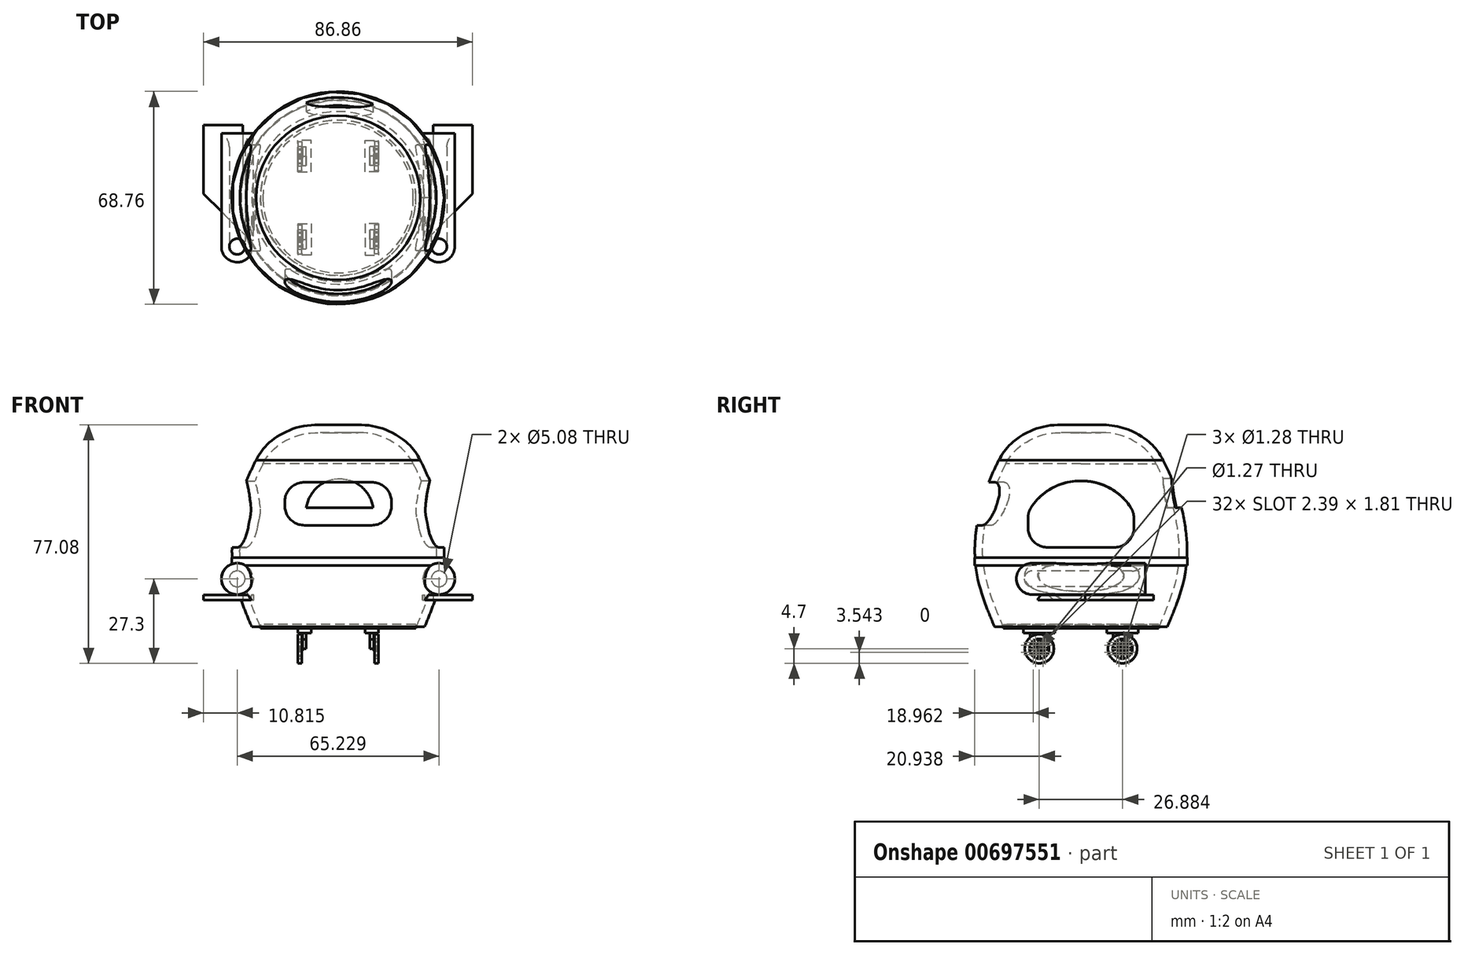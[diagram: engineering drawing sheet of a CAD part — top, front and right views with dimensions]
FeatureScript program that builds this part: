
annotation { "Feature Type Name" : "Feature", "Feature Type Description" : "" }
export const myFeature = defineFeature(function(context is Context, id is Id, definition is map)
    precondition{}
    {
        {
            var Q0;
            Q0=qCreatedBy(makeId("Front.planeOp"),FACE);
            var sketch = newSketch(context, id + "F0", { "sketchPlane" : qUnion([Q0])});
            skFitSpline(sketch, "E0", {"points": [v(-26.52, 28.24) * mm, v(-31.57, 16.07) * mm, v(-34.1, -5.28) * mm, v(-27.9, -25.71) * mm], "startDerivative": vector(-19.07, -39.25) * mm, "endDerivative": vector(23, -55.14) * mm});
            skLineSegment(sketch, "E1", {"start": v(0, 51.66) * mm, "end": v(0, -63.37) * mm, "construction": true});
            skLineSegment(sketch, "E2", {"start": v(0, 43.62) * mm, "end": v(0, -25.71) * mm});
            skFitSpline(sketch, "E3", {"points": [v(-26.52, 28.24) * mm, v(-24.68, 31.2) * mm, v(-21.66, 34.36) * mm, v(-16.76, 37.41) * mm, v(-10.13, 39.4) * mm, v(-3.92, 39.57) * mm, v(0, 39.62) * mm], "startDerivative": vector(11.97, 21.05) * mm, "endDerivative": vector(33.65, 0.28) * mm});
            skLineSegment(sketch, "E4", {"start": v(-27.9, -25.71) * mm, "end": v(0, -25.71) * mm});
            skSolve(sketch);
        }
        {
            var Q0;
            Q0=makeQuery(id+"F0.imprint","IMPRINT",FACE,{"disambiguationData":[TD([[makeQuery(id+"F0.imprint","IMPRINT",EDGE,{"derivedFrom":sQuery(id+"F0.wireOp",EDGE,"E0")}),1.0]])]});
            var Q1;
            Q1=sQuery(id+"F0.wireOp",EDGE,"E2");
            revolve(context, id + "F1", {"entities" : qUnion([Q0]), "axis" : qUnion([Q1]), "revolveType" : RevolveType.FULL});
        }
        {
            var Q0;
            Q0=makeQuery(id+"F1.opRevolve","SWEPT_FACE",FACE,{"disambiguationData":[OSD([sQuery(id+"F0.wireOp",EDGE,"E4")])]});
            shell(context, id + "F2", {"entities" : qUnion([Q0]), "thickness" : 2.54 * mm});
        }
        {
            var Q0;
            Q0=qCreatedBy(makeId("Top.planeOp"),FACE);
            cPlane(context, id + "F3", {"entities" : qUnion([Q0]), "cplaneType" : CPlaneType.OFFSET, "offset" : 26.16 * mm, "oppositeDirection" : true, "width" : 152.4 * mm, "height" : 152.4 * mm});
        }
        {
            var Q0;
            Q0=qCreatedBy(id+"F3.planeOp",FACE);
            var sketch = newSketch(context, id + "F4", { "sketchPlane" : qUnion([Q0])});
            skPoint(sketch, "E5.middle", {"position": v(0, 0) * mm});
            skCircle(sketch, "E6", {"center": v(0, 0) * mm, "radius": 25.04 * mm});
            skSolve(sketch);
        }
        {
            var Q0;
            Q0=qCreatedBy(makeId("Front.planeOp"),FACE);
            cPlane(context, id + "F5", {"entities" : qUnion([Q0]), "cplaneType" : CPlaneType.OFFSET, "offset" : 28.45 * mm, "width" : 152.4 * mm, "height" : 152.4 * mm});
        }
        {
            var Q0;
            Q0=qCreatedBy(id+"F5.planeOp",FACE);
            var sketch = newSketch(context, id + "F6", { "sketchPlane" : qUnion([Q0])});
            skLineSegment(sketch, "E7.bottom", {"start": v(-10.9, 21.05) * mm, "end": v(10.9, 21.05) * mm});
            skLineSegment(sketch, "E7.top", {"start": v(-10.9, 7.16) * mm, "end": v(10.9, 7.16) * mm});
            skLineSegment(sketch, "E7.left", {"start": v(-17.26, 14.7) * mm, "end": v(-17.26, 13.51) * mm});
            skLineSegment(sketch, "E7.right", {"start": v(17.26, 14.7) * mm, "end": v(17.26, 13.51) * mm});
            skPoint(sketch, "E7.middle", {"position": v(0, 14.1) * mm});
            skPoint(sketch, "E8.visualSharp", {"position": v(-17.26, 21.05) * mm});
            skArc(sketch, "E8.filletArc", {"start": v(-10.9, 21.05) * mm, "mid": v(-15.4, 19.19) * mm, "end": v(-17.26, 14.7) * mm});
            skPoint(sketch, "E9.visualSharp", {"position": v(17.26, 21.05) * mm});
            skArc(sketch, "E9.filletArc", {"start": v(17.26, 14.7) * mm, "mid": v(15.4, 19.19) * mm, "end": v(10.9, 21.05) * mm});
            skPoint(sketch, "E10.visualSharp", {"position": v(17.26, 7.16) * mm});
            skArc(sketch, "E10.filletArc", {"start": v(10.9, 7.16) * mm, "mid": v(15.4, 9.02) * mm, "end": v(17.26, 13.51) * mm});
            skPoint(sketch, "E11.visualSharp", {"position": v(-17.26, 7.16) * mm});
            skArc(sketch, "E11.filletArc", {"start": v(-17.26, 13.51) * mm, "mid": v(-15.4, 9.02) * mm, "end": v(-10.9, 7.16) * mm});
            skSolve(sketch);
        }
        {
            var Q0;
            Q0 = qSketchRegion(id + "F6", true);
            extrude(context, id + "F7", {"entities" : qUnion([Q0]), "operationType" : NewBodyOperationType.REMOVE, "endBound" : BoundingType.SYMMETRIC, "oppositeDirection" : true, "depth" : 12.7 * mm, "offsetDistance" : 25.4 * mm});
        }
        {
            var Q0;
            Q0=qCreatedBy(makeId("Right.planeOp"),FACE);
            cPlane(context, id + "F8", {"entities" : qUnion([Q0]), "cplaneType" : CPlaneType.OFFSET, "offset" : 30.48 * mm, "width" : 152.4 * mm, "height" : 152.4 * mm});
        }
        {
            var Q0;
            Q0=qCreatedBy(id+"F8.planeOp",FACE);
            var sketch = newSketch(context, id + "F9", { "sketchPlane" : qUnion([Q0])});
            skArc(sketch, "E12", {"start": v(0, 21.5) * mm, "mid": v(-9.18, 19.27) * mm, "end": v(-16.1, 12.86) * mm});
            skArc(sketch, "E13.MirrorCS", {"start": v(0, 21.5) * mm, "mid": v(9.18, 19.27) * mm, "end": v(16.1, 12.86) * mm});
            skLineSegment(sketch, "E14", {"start": v(-17.11, 9.43) * mm, "end": v(-17.11, 6.35) * mm});
            skLineSegment(sketch, "E15", {"start": v(-10.76, 0) * mm, "end": v(10.76, 0) * mm});
            skLineSegment(sketch, "E16", {"start": v(17.11, 6.35) * mm, "end": v(17.11, 9.43) * mm});
            skLineSegment(sketch, "E17.bottom", {"start": v(0.3, 21.5) * mm, "end": v(-0.3, 21.5) * mm});
            skLineSegment(sketch, "E17.top", {"start": v(0.3, 0) * mm, "end": v(-0.3, 0) * mm});
            skPoint(sketch, "E17.middle", {"position": v(0, 10.75) * mm});
            skPoint(sketch, "E18.visualSharp", {"position": v(-17.11, 11.09) * mm});
            skArc(sketch, "E18.filletArc", {"start": v(-16.1, 12.86) * mm, "mid": v(-16.86, 11.22) * mm, "end": v(-17.11, 9.43) * mm});
            skPoint(sketch, "E19.visualSharp", {"position": v(17.11, 11.09) * mm});
            skArc(sketch, "E19.filletArc", {"start": v(17.11, 9.43) * mm, "mid": v(16.86, 11.22) * mm, "end": v(16.1, 12.86) * mm});
            skPoint(sketch, "E20.visualSharp", {"position": v(-17.11, 0) * mm});
            skArc(sketch, "E20.filletArc", {"start": v(-17.11, 6.35) * mm, "mid": v(-15.25, 1.86) * mm, "end": v(-10.76, 0) * mm});
            skPoint(sketch, "E21.visualSharp", {"position": v(17.11, 0) * mm});
            skArc(sketch, "E21.filletArc", {"start": v(10.76, 0) * mm, "mid": v(15.25, 1.86) * mm, "end": v(17.11, 6.35) * mm});
            skSolve(sketch);
        }
        {
            var Q0;
            Q0=makeQuery(id+"F9.imprint","IMPRINT",FACE,{"disambiguationData":[TD([[makeQuery(id+"F9.imprint","IMPRINT",EDGE,{"derivedFrom":sQuery(id+"F9.wireOp",EDGE,"E14")}),1.0]])]});
            extrude(context, id + "F10", {"entities" : qUnion([Q0]), "operationType" : NewBodyOperationType.REMOVE, "endBound" : BoundingType.SYMMETRIC, "depth" : 10.87 * mm, "offsetDistance" : 25.4 * mm});
        }
        {
            var Q0;
            Q0=qCreatedBy(makeId("Right.planeOp"),FACE);
            cPlane(context, id + "F11", {"entities" : qUnion([Q0]), "cplaneType" : CPlaneType.OFFSET, "offset" : 30.48 * mm, "oppositeDirection" : true, "width" : 152.4 * mm, "height" : 152.4 * mm});
        }
        {
            var Q0;
            Q0=qCreatedBy(id+"F11.planeOp",FACE);
            var sketch = newSketch(context, id + "F12", { "sketchPlane" : qUnion([Q0])});
            skArc(sketch, "E22", {"start": v(0.24, 21.49) * mm, "mid": v(-9.07, 19.32) * mm, "end": v(-16.1, 12.85) * mm});
            skArc(sketch, "E23.MirrorCS", {"start": v(-0.24, 21.49) * mm, "mid": v(9.07, 19.32) * mm, "end": v(16.1, 12.85) * mm});
            skLineSegment(sketch, "E24", {"start": v(-17.11, 9.42) * mm, "end": v(-17.11, 6.34) * mm});
            skLineSegment(sketch, "E25", {"start": v(-10.76, -0.01) * mm, "end": v(10.76, -0.01) * mm});
            skLineSegment(sketch, "E26", {"start": v(17.11, 6.34) * mm, "end": v(17.11, 9.42) * mm});
            skLineSegment(sketch, "E27.bottom", {"start": v(0.3, 21.5) * mm, "end": v(-0.3, 21.5) * mm});
            skLineSegment(sketch, "E27.top", {"start": v(0.3, -0.01) * mm, "end": v(-0.3, -0.01) * mm});
            skPoint(sketch, "E27.middle", {"position": v(0, 10.74) * mm});
            skPoint(sketch, "E28.visualSharp", {"position": v(-17.11, 11.08) * mm});
            skArc(sketch, "E28.filletArc", {"start": v(-16.1, 12.85) * mm, "mid": v(-16.86, 11.2) * mm, "end": v(-17.11, 9.42) * mm});
            skPoint(sketch, "E29.visualSharp", {"position": v(17.11, 11.08) * mm});
            skArc(sketch, "E29.filletArc", {"start": v(17.11, 9.42) * mm, "mid": v(16.86, 11.2) * mm, "end": v(16.1, 12.85) * mm});
            skPoint(sketch, "E30.visualSharp", {"position": v(-17.11, -0.01) * mm});
            skArc(sketch, "E30.filletArc", {"start": v(-17.11, 6.34) * mm, "mid": v(-15.25, 1.85) * mm, "end": v(-10.76, -0.01) * mm});
            skPoint(sketch, "E31.visualSharp", {"position": v(17.11, -0.01) * mm});
            skArc(sketch, "E31.filletArc", {"start": v(10.76, -0.01) * mm, "mid": v(15.25, 1.85) * mm, "end": v(17.11, 6.34) * mm});
            skSolve(sketch);
        }
        {
            var Q0;
            Q0 = qSketchRegion(id + "F12", true);
            extrude(context, id + "F13", {"entities" : qUnion([Q0]), "operationType" : NewBodyOperationType.REMOVE, "endBound" : BoundingType.SYMMETRIC, "oppositeDirection" : true, "depth" : 10.87 * mm, "offsetDistance" : 25.4 * mm});
        }
        {
            var Q0;
            Q0=qCreatedBy(makeId("Front.planeOp"),FACE);
            var sketch = newSketch(context, id + "F14", { "sketchPlane" : qUnion([Q0])});
            skLineSegment(sketch, "E32", {"start": v(0, 0) * mm, "end": v(0, -10.16) * mm, "construction": true});
            skCircle(sketch, "E33", {"center": v(-32.61, -10.16) * mm, "radius": 5.08 * mm});
            skCircle(sketch, "E34.MirrorC", {"center": v(32.61, -10.16) * mm, "radius": 5.08 * mm});
            skSolve(sketch);
        }
        {
            var Q0;
            Q0 = qSketchRegion(id + "F14", true);
            extrude(context, id + "F15", {"entities" : qUnion([Q0]), "operationType" : NewBodyOperationType.ADD, "endBound" : BoundingType.SYMMETRIC, "oppositeDirection" : true, "depth" : 41.66 * mm, "offsetDistance" : 25.4 * mm});
        }
        {
            var Q0;
            Q0=makeQuery(id+"F15.opExtrude","CAP_EDGE",EDGE,{"disambiguationData":[OSD([sQuery(id+"F14.wireOp",EDGE,"E33")])],"isStart":true});
            fillet(context, id + "F16", {"entities" : qUnion([Q0]), "radius" : 5.08 * mm, "tangentPropagation" : true, "allowEdgeOverflow" : false});
        }
        {
            var Q0;
            Q0=makeQuery(id+"F15.opExtrude","CAP_EDGE",EDGE,{"disambiguationData":[OSD([sQuery(id+"F14.wireOp",EDGE,"E34.MirrorC")])],"isStart":true});
            fillet(context, id + "F17", {"entities" : qUnion([Q0]), "radius" : 5.08 * mm, "tangentPropagation" : true, "allowEdgeOverflow" : false});
        }
        {
            var Q0;
            Q0=makeQuery(id+"F15.opExtrude","CAP_FACE",FACE,{"disambiguationData":[OSD([sQuery(id+"F14.wireOp",EDGE,"E34.MirrorC")])],"isStart":false});
            var Q1;
            Q1=makeQuery(id+"F15.opExtrude","CAP_FACE",FACE,{"disambiguationData":[OSD([sQuery(id+"F14.wireOp",EDGE,"E33")])],"isStart":false});
            shell(context, id + "F18", {"entities" : qUnion([Q0, Q1]), "thickness" : 2.54 * mm});
        }
        {
            var Q0;
            {var subQ0=sQuery(id+"F14.wireOp",EDGE,"E34.MirrorC");Q0=makeQuery(id+"F18.opShell","OFFSET_EDGE",EDGE,{"disambiguationData":[OSD([subQ0]),TDD([makeQuery(id+"F15.opExtrude","CAP_EDGE",EDGE,{"disambiguationData":[OSD([subQ0])],"isStart":false})])]});}
            var Q1;
            {var subQ0=sQuery(id+"F14.wireOp",EDGE,"E33");Q1=makeQuery(id+"F18.opShell","OFFSET_EDGE",EDGE,{"disambiguationData":[OSD([subQ0]),TDD([makeQuery(id+"F15.opExtrude","CAP_EDGE",EDGE,{"disambiguationData":[OSD([subQ0])],"isStart":false})])]});}
            fillet(context, id + "F19", {"entities" : qUnion([Q0, Q1]), "radius" : 5.08 * mm, "tangentPropagation" : true, "allowEdgeOverflow" : false});
        }
        {
            var Q0;
            Q0=qCreatedBy(makeId("Top.planeOp"),FACE);
            cPlane(context, id + "F20", {"entities" : qUnion([Q0]), "cplaneType" : CPlaneType.OFFSET, "offset" : 15 * mm, "oppositeDirection" : true, "width" : 152.4 * mm, "height" : 152.4 * mm});
        }
        {
            var Q0;
            Q0 = qSketchRegion(id + "F4", true);
            extrude(context, id + "F21", {"entities" : qUnion([Q0]), "depth" : 1.27 * mm, "offsetDistance" : 25.4 * mm});
        }
        {
            var Q0;
            Q0=qCreatedBy(id+"F3.planeOp",FACE);
            var sketch = newSketch(context, id + "F22", { "sketchPlane" : qUnion([Q0])});
            skLineSegment(sketch, "E35.MirrorCS", {"start": v(-8.75, -18.52) * mm, "end": v(-13, -18.52) * mm});
            skLineSegment(sketch, "E36", {"start": v(-13, -8.36) * mm, "end": v(-8.75, -8.36) * mm});
            skLineSegment(sketch, "E37.trimOffspring", {"start": v(-8.75, -8.36) * mm, "end": v(-8.75, -18.52) * mm});
            skLineSegment(sketch, "E38.trimOffspring", {"start": v(-13, -8.36) * mm, "end": v(-13, -18.52) * mm});
            skLineSegment(sketch, "E39.MirrorCS", {"start": v(8.75, -8.36) * mm, "end": v(8.75, -18.52) * mm});
            skLineSegment(sketch, "E40.MirrorCS", {"start": v(13, -8.36) * mm, "end": v(13, -18.52) * mm});
            skLineSegment(sketch, "E41.MirrorCS", {"start": v(8.75, -18.52) * mm, "end": v(13, -18.52) * mm});
            skLineSegment(sketch, "E42.MirrorCS", {"start": v(13, -8.36) * mm, "end": v(8.75, -8.36) * mm});
            skLineSegment(sketch, "E43.MirrorCS", {"start": v(-13, 8.36) * mm, "end": v(-8.75, 8.36) * mm});
            skLineSegment(sketch, "E44.MirrorCS", {"start": v(-8.75, 18.52) * mm, "end": v(-13, 18.52) * mm});
            skLineSegment(sketch, "E45.MirrorCS", {"start": v(-13, 8.36) * mm, "end": v(-13, 18.52) * mm});
            skLineSegment(sketch, "E46.MirrorCS", {"start": v(-8.75, 8.36) * mm, "end": v(-8.75, 18.52) * mm});
            skLineSegment(sketch, "E47.MirrorCS", {"start": v(8.75, 8.36) * mm, "end": v(8.75, 18.52) * mm});
            skLineSegment(sketch, "E48.MirrorCS", {"start": v(8.75, 18.52) * mm, "end": v(13, 18.52) * mm});
            skLineSegment(sketch, "E49.MirrorCS", {"start": v(13, 8.36) * mm, "end": v(13, 18.52) * mm});
            skLineSegment(sketch, "E50.MirrorCS", {"start": v(13, 8.36) * mm, "end": v(8.75, 8.36) * mm});
            skSolve(sketch);
        }
        {
            var Q0;
            Q0 = qSketchRegion(id + "F22", true);
            extrude(context, id + "F23", {"entities" : qUnion([Q0]), "operationType" : NewBodyOperationType.ADD, "oppositeDirection" : true, "depth" : 1.52 * mm, "offsetDistance" : 25.4 * mm});
        }
        {
            var Q0;
            Q0=makeQuery(id+"F23.opExtrude","CAP_FACE",FACE,{"disambiguationData":[OSD([sQuery(id+"F22.wireOp",EDGE,"E35.MirrorCS"),sQuery(id+"F22.wireOp",EDGE,"E36"),sQuery(id+"F22.wireOp",EDGE,"E37.trimOffspring"),sQuery(id+"F22.wireOp",EDGE,"E38.trimOffspring")])],"isStart":false});
            var sketch = newSketch(context, id + "F24", { "sketchPlane" : qUnion([Q0])});
            skLineSegment(sketch, "E51.bottom", {"start": v(-11.45, 10.4) * mm, "end": v(-10.3, 10.4) * mm});
            skLineSegment(sketch, "E51.top", {"start": v(-11.45, 16.48) * mm, "end": v(-10.3, 16.48) * mm});
            skLineSegment(sketch, "E51.left", {"start": v(-11.45, 10.4) * mm, "end": v(-11.45, 16.48) * mm});
            skLineSegment(sketch, "E51.right", {"start": v(-10.3, 10.4) * mm, "end": v(-10.3, 16.48) * mm});
            skPoint(sketch, "E51.middle", {"position": v(-10.87, 13.44) * mm});
            skPoint(sketch, "E51.middle.positionSnap0", {"position": v(-10.87, 18.52) * mm});
            skPoint(sketch, "E51.middle.positionSnap1", {"position": v(-13, 13.44) * mm});
            skPoint(sketch, "E51.centerSnap0", {"position": v(-10.87, 18.52) * mm});
            skPoint(sketch, "E52.MirrorP", {"position": v(-10.87, -13.44) * mm});
            skLineSegment(sketch, "E53.MirrorCS", {"start": v(-11.45, -10.4) * mm, "end": v(-11.45, -16.48) * mm});
            skLineSegment(sketch, "E54.MirrorCS", {"start": v(-11.45, -10.4) * mm, "end": v(-10.3, -10.4) * mm});
            skLineSegment(sketch, "E55.MirrorCS", {"start": v(-10.3, -10.4) * mm, "end": v(-10.3, -16.48) * mm});
            skLineSegment(sketch, "E56.MirrorCS", {"start": v(-11.45, -16.48) * mm, "end": v(-10.3, -16.48) * mm});
            skLineSegment(sketch, "E57.MirrorCS", {"start": v(10.3, 10.4) * mm, "end": v(10.3, 16.48) * mm});
            skLineSegment(sketch, "E58.MirrorCS", {"start": v(11.45, 10.4) * mm, "end": v(11.45, 16.48) * mm});
            skLineSegment(sketch, "E59.MirrorCS", {"start": v(11.45, 10.4) * mm, "end": v(10.3, 10.4) * mm});
            skLineSegment(sketch, "E60.MirrorCS", {"start": v(11.45, 16.48) * mm, "end": v(10.3, 16.48) * mm});
            skLineSegment(sketch, "E61.MirrorCS", {"start": v(11.45, -10.4) * mm, "end": v(10.3, -10.4) * mm});
            skLineSegment(sketch, "E62.MirrorCS", {"start": v(11.45, -16.48) * mm, "end": v(10.3, -16.48) * mm});
            skLineSegment(sketch, "E63.MirrorCS", {"start": v(11.45, -10.4) * mm, "end": v(11.45, -16.48) * mm});
            skLineSegment(sketch, "E64.MirrorCS", {"start": v(10.3, -10.4) * mm, "end": v(10.3, -16.48) * mm});
            skSolve(sketch);
        }
        {
            var Q0;
            Q0 = qSketchRegion(id + "F24", true);
            extrude(context, id + "F25", {"entities" : qUnion([Q0]), "operationType" : NewBodyOperationType.ADD, "depth" : 5.08 * mm, "offsetDistance" : 25.4 * mm});
        }
        {
            var Q0;
            Q0=makeQuery(id+"F25.opExtrude","CAP_EDGE",EDGE,{"disambiguationData":[OSD([sQuery(id+"F24.wireOp",EDGE,"E54.MirrorCS")])],"isStart":false});
            var Q1;
            Q1=makeQuery(id+"F25.opExtrude","CAP_EDGE",EDGE,{"disambiguationData":[OSD([sQuery(id+"F24.wireOp",EDGE,"E56.MirrorCS")])],"isStart":false});
            var Q2;
            Q2=makeQuery(id+"F25.opExtrude","CAP_EDGE",EDGE,{"disambiguationData":[OSD([sQuery(id+"F24.wireOp",EDGE,"E51.top")])],"isStart":false});
            var Q3;
            Q3=makeQuery(id+"F25.opExtrude","CAP_EDGE",EDGE,{"disambiguationData":[OSD([sQuery(id+"F24.wireOp",EDGE,"E51.bottom")])],"isStart":false});
            var Q4;
            Q4=makeQuery(id+"F25.opExtrude","CAP_EDGE",EDGE,{"disambiguationData":[OSD([sQuery(id+"F24.wireOp",EDGE,"E62.MirrorCS")])],"isStart":false});
            var Q5;
            Q5=makeQuery(id+"F25.opExtrude","CAP_EDGE",EDGE,{"disambiguationData":[OSD([sQuery(id+"F24.wireOp",EDGE,"E61.MirrorCS")])],"isStart":false});
            var Q6;
            Q6=makeQuery(id+"F25.opExtrude","CAP_EDGE",EDGE,{"disambiguationData":[OSD([sQuery(id+"F24.wireOp",EDGE,"E59.MirrorCS")])],"isStart":false});
            var Q7;
            Q7=makeQuery(id+"F25.opExtrude","CAP_EDGE",EDGE,{"disambiguationData":[OSD([sQuery(id+"F24.wireOp",EDGE,"E60.MirrorCS")])],"isStart":false});
            chamfer(context, id + "F26", {"entities" : qUnion([Q0, Q1, Q2, Q3, Q4, Q5, Q6, Q7]), "width" : 3.05 * mm, "tangentPropagation" : true});
        }
        {
            var Q0;
            Q0=makeQuery(id+"F25.opExtrude","SWEPT_FACE",FACE,{"disambiguationData":[OSD([sQuery(id+"F24.wireOp",EDGE,"E51.left")])]});
            var sketch = newSketch(context, id + "F27", { "sketchPlane" : qUnion([Q0])});
            skCircle(sketch, "E65", {"center": v(13.44, -32.76) * mm, "radius": 0.64 * mm});
            skSolve(sketch);
        }
        {
            var Q0;
            Q0 = qSketchRegion(id + "F27", true);
            extrude(context, id + "F28", {"entities" : qUnion([Q0]), "operationType" : NewBodyOperationType.ADD, "depth" : 0.25 * mm, "offsetDistance" : 25.4 * mm});
        }
        {
            var Q0;
            Q0=makeQuery(id+"F28.opExtrude","CAP_FACE",FACE,{"disambiguationData":[OSD([sQuery(id+"F27.wireOp",EDGE,"E65")])],"isStart":false});
            var sketch = newSketch(context, id + "F29", { "sketchPlane" : qUnion([Q0])});
            skCircle(sketch, "E66", {"center": v(13.44, -32.76) * mm, "radius": 4.7 * mm});
            skArc(sketch, "E67.0", {"start": v(13.19, -29.6) * mm, "mid": v(12.23, -29.82) * mm, "end": v(11.38, -30.34) * mm});
            skArc(sketch, "E68", {"start": v(13.19, -31.9) * mm, "mid": v(13.1, -31.94) * mm, "end": v(13.02, -31.98) * mm});
            skLineSegment(sketch, "E69.0", {"start": v(13.7, -31.9) * mm, "end": v(13.7, -29.6) * mm});
            skLineSegment(sketch, "E70.0", {"start": v(13.19, -31.9) * mm, "end": v(13.19, -29.6) * mm});
            skLineSegment(sketch, "E71", {"start": v(13.7, -33.61) * mm, "end": v(13.7, -35.93) * mm});
            skLineSegment(sketch, "E72", {"start": v(13.19, -33.61) * mm, "end": v(13.19, -35.93) * mm});
            skArc(sketch, "E73.trimOffspring", {"start": v(13.7, -33.61) * mm, "mid": v(13.78, -33.58) * mm, "end": v(13.87, -33.54) * mm});
            skArc(sketch, "E74.trimOffspring", {"start": v(13.7, -35.93) * mm, "mid": v(14.66, -35.7) * mm, "end": v(15.5, -35.18) * mm});
            skLineSegment(sketch, "E75.0", {"start": v(8.74, -33.01) * mm, "end": v(8.75, -33.01) * mm});
            skLineSegment(sketch, "E76.0", {"start": v(8.74, -32.5) * mm, "end": v(8.75, -32.5) * mm});
            skLineSegment(sketch, "E77.trimOffspring", {"start": v(10.27, -32.5) * mm, "end": v(12.59, -32.5) * mm});
            skLineSegment(sketch, "E78.trimOffspring", {"start": v(10.27, -33.01) * mm, "end": v(12.59, -33.01) * mm});
            skLineSegment(sketch, "E79.trimOffspring", {"start": v(18.14, -32.5) * mm, "end": v(18.14, -32.5) * mm});
            skLineSegment(sketch, "E80.trimOffspring", {"start": v(18.14, -33.01) * mm, "end": v(18.14, -33.01) * mm});
            skLineSegment(sketch, "E81.trimOffspring", {"start": v(14.3, -32.5) * mm, "end": v(16.61, -32.5) * mm});
            skLineSegment(sketch, "E82.trimOffspring", {"start": v(14.3, -33.01) * mm, "end": v(16.61, -33.01) * mm});
            skArc(sketch, "E83.trimOffspring", {"start": v(10.27, -33.01) * mm, "mid": v(10.5, -33.98) * mm, "end": v(11.02, -34.82) * mm});
            skArc(sketch, "E84.trimOffspring", {"start": v(16.61, -32.5) * mm, "mid": v(16.38, -31.54) * mm, "end": v(15.86, -30.7) * mm});
            skArc(sketch, "E85.trimOffspring", {"start": v(12.59, -33.01) * mm, "mid": v(12.62, -33.1) * mm, "end": v(12.66, -33.18) * mm});
            skLineSegment(sketch, "E86.0", {"start": v(15.51, -30.33) * mm, "end": v(13.87, -31.98) * mm});
            skLineSegment(sketch, "E87.0", {"start": v(15.87, -30.7) * mm, "end": v(14.22, -32.34) * mm});
            skLineSegment(sketch, "E88.trimOffspring", {"start": v(12.66, -33.18) * mm, "end": v(11.01, -34.83) * mm});
            skLineSegment(sketch, "E89.trimOffspring", {"start": v(13.02, -33.54) * mm, "end": v(11.37, -35.19) * mm});
            skArc(sketch, "E90.trimOffspring", {"start": v(13.02, -33.54) * mm, "mid": v(13.1, -33.58) * mm, "end": v(13.19, -33.61) * mm});
            skArc(sketch, "E91.trimOffspring", {"start": v(13.87, -31.98) * mm, "mid": v(13.78, -31.94) * mm, "end": v(13.7, -31.9) * mm});
            skArc(sketch, "E92.trimOffspring", {"start": v(11.38, -35.18) * mm, "mid": v(12.23, -35.7) * mm, "end": v(13.19, -35.93) * mm});
            skArc(sketch, "E93.trimOffspring", {"start": v(15.5, -30.34) * mm, "mid": v(14.66, -29.82) * mm, "end": v(13.7, -29.6) * mm});
            skArc(sketch, "E94.trimOffspring", {"start": v(14.3, -32.5) * mm, "mid": v(14.26, -32.42) * mm, "end": v(14.22, -32.34) * mm});
            skLineSegment(sketch, "E95.0", {"start": v(11.01, -30.7) * mm, "end": v(12.66, -32.34) * mm});
            skLineSegment(sketch, "E96.0", {"start": v(11.37, -30.33) * mm, "end": v(13.02, -31.98) * mm});
            skArc(sketch, "E97.trimOffspring", {"start": v(12.66, -32.34) * mm, "mid": v(12.62, -32.42) * mm, "end": v(12.59, -32.5) * mm});
            skLineSegment(sketch, "E98.trimOffspring", {"start": v(13.87, -33.54) * mm, "end": v(15.51, -35.19) * mm});
            skLineSegment(sketch, "E99.trimOffspring", {"start": v(14.22, -33.18) * mm, "end": v(15.87, -34.83) * mm});
            skArc(sketch, "E100.trimOffspring", {"start": v(14.22, -33.18) * mm, "mid": v(14.26, -33.1) * mm, "end": v(14.3, -33.01) * mm});
            skArc(sketch, "E101.trimOffspring", {"start": v(11.02, -30.7) * mm, "mid": v(10.5, -31.54) * mm, "end": v(10.27, -32.5) * mm});
            skArc(sketch, "E102.trimOffspring", {"start": v(15.86, -34.82) * mm, "mid": v(16.38, -33.98) * mm, "end": v(16.61, -33.01) * mm});
            skSolve(sketch);
        }
        {
            var Q0;
            {var subQ16=sQuery(id+"F29.wireOp",EDGE,"E67.0");Q0=makeQuery(id+"F29.imprint","IMPRINT",FACE,{"disambiguationData":[TD([[makeQuery(id+"F29.imprint","IMPRINT",EDGE,{"derivedFrom":subQ16}),-1.0]])]});}
            extrude(context, id + "F30", {"entities" : qUnion([Q0]), "depth" : 1.27 * mm, "offsetDistance" : 25.4 * mm});
        }
        {
            var Q0;
            Q0=qCreatedBy(makeId("Right.planeOp"),FACE);
            cPlane(context, id + "F31", {"entities" : qUnion([Q0]), "cplaneType" : CPlaneType.OFFSET, "offset" : 30.73 * mm, "oppositeDirection" : true, "width" : 152.4 * mm, "height" : 152.4 * mm});
        }
        {
            var Q0;
            Q0=qCreatedBy(id+"F31.planeOp",FACE);
            var sketch = newSketch(context, id + "F32", { "sketchPlane" : qUnion([Q0])});
            skLineSegment(sketch, "E103.bottom", {"start": v(23.47, -15.31) * mm, "end": v(-13.94, -15.31) * mm});
            skLineSegment(sketch, "E103.top", {"start": v(23.47, -16.99) * mm, "end": v(-13.94, -16.99) * mm});
            skLineSegment(sketch, "E103.left", {"start": v(23.47, -15.31) * mm, "end": v(23.47, -16.99) * mm});
            skPoint(sketch, "E103.middle", {"position": v(0, -16.15) * mm});
            skLineSegment(sketch, "E104", {"start": v(-13.94, -15.31) * mm, "end": v(-13.94, -16.99) * mm});
            skSolve(sketch);
        }
        {
            var Q0;
            Q0 = qSketchRegion(id + "F32", true);
            extrude(context, id + "F33", {"entities" : qUnion([Q0]), "operationType" : NewBodyOperationType.ADD, "oppositeDirection" : true, "depth" : 12.7 * mm, "offsetDistance" : 25.4 * mm});
        }
        {
            var Q0;
            {var subQ0=sQuery(id+"F32.wireOp",EDGE,"E103.bottom");var subQ1=sQuery(id+"F32.wireOp",EDGE,"E104");var subQ2=sQuery(id+"F32.wireOp",EDGE,"E103.top");Q0=makeQuery(id+"F33.boolean.opBoolean","SPLIT",FACE,{"disambiguationData":[TD([makeQuery(id+"F33.opExtrude","SWEPT_FACE",FACE,{"disambiguationData":[OSD([subQ1])]})])],"derivedFrom":makeQuery(id+"F33.opExtrude","CAP_FACE",FACE,{"disambiguationData":[OSD([subQ0,subQ2,sQuery(id+"F32.wireOp",EDGE,"E103.left"),subQ1])],"isStart":true})});}
            var sketch = newSketch(context, id + "F34", { "sketchPlane" : qUnion([Q0])});
            skLineSegment(sketch, "E105", {"start": v(-13.94, -15.31) * mm, "end": v(-13.94, -16.99) * mm});
            skLineSegment(sketch, "E106", {"start": v(-13.94, -16.99) * mm, "end": v(-6.12, -16.99) * mm});
            skLineSegment(sketch, "E107", {"start": v(-6.12, -16.99) * mm, "end": v(-8.56, -15.31) * mm});
            skLineSegment(sketch, "E108", {"start": v(-8.56, -15.31) * mm, "end": v(-13.94, -15.31) * mm});
            skSolve(sketch);
        }
        {
            var Q0;
            Q0 = qSketchRegion(id + "F34", true);
            extrude(context, id + "F35", {"entities" : qUnion([Q0]), "operationType" : NewBodyOperationType.ADD, "depth" : 3.48 * mm, "offsetDistance" : 25.4 * mm});
        }
        {
            var Q0;
            Q0=makeQuery(id+"F25.opExtrude","SWEPT_FACE",FACE,{"disambiguationData":[OSD([sQuery(id+"F24.wireOp",EDGE,"E53.MirrorCS")])]});
            var sketch = newSketch(context, id + "F36", { "sketchPlane" : qUnion([Q0])});
            skCircle(sketch, "E109", {"center": v(-13.44, -32.76) * mm, "radius": 0.64 * mm});
            skSolve(sketch);
        }
        {
            var Q0;
            Q0 = qSketchRegion(id + "F36", true);
            extrude(context, id + "F37", {"entities" : qUnion([Q0]), "operationType" : NewBodyOperationType.ADD, "depth" : 0.25 * mm, "offsetDistance" : 25.4 * mm});
        }
        {
            var Q0;
            Q0=makeQuery(id+"F25.opExtrude","SWEPT_FACE",FACE,{"disambiguationData":[OSD([sQuery(id+"F24.wireOp",EDGE,"E63.MirrorCS")])]});
            var sketch = newSketch(context, id + "F38", { "sketchPlane" : qUnion([Q0])});
            skCircle(sketch, "E110", {"center": v(13.44, -32.76) * mm, "radius": 0.64 * mm});
            skSolve(sketch);
        }
        {
            var Q0;
            Q0 = qSketchRegion(id + "F38", true);
            extrude(context, id + "F39", {"entities" : qUnion([Q0]), "operationType" : NewBodyOperationType.ADD, "depth" : 0.25 * mm, "offsetDistance" : 25.4 * mm});
        }
        {
            var Q0;
            Q0=makeQuery(id+"F25.opExtrude","SWEPT_FACE",FACE,{"disambiguationData":[OSD([sQuery(id+"F24.wireOp",EDGE,"E58.MirrorCS")])]});
            var sketch = newSketch(context, id + "F40", { "sketchPlane" : qUnion([Q0])});
            skCircle(sketch, "E111", {"center": v(-13.44, -32.76) * mm, "radius": 0.63 * mm});
            skSolve(sketch);
        }
        {
            var Q0;
            Q0 = qSketchRegion(id + "F40", true);
            extrude(context, id + "F41", {"entities" : qUnion([Q0]), "operationType" : NewBodyOperationType.ADD, "depth" : 0.25 * mm, "offsetDistance" : 25.4 * mm});
        }
        {
            var Q0;
            Q0=makeQuery(id+"F37.opExtrude","CAP_FACE",FACE,{"disambiguationData":[OSD([sQuery(id+"F36.wireOp",EDGE,"E109")])],"isStart":false});
            var sketch = newSketch(context, id + "F42", { "sketchPlane" : qUnion([Q0])});
            skCircle(sketch, "E112", {"center": v(-13.44, -32.76) * mm, "radius": 4.7 * mm});
            skArc(sketch, "E113.0", {"start": v(-13.7, -29.6) * mm, "mid": v(-14.66, -29.82) * mm, "end": v(-15.5, -30.34) * mm});
            skArc(sketch, "E114", {"start": v(-13.7, -31.9) * mm, "mid": v(-13.78, -31.94) * mm, "end": v(-13.87, -31.98) * mm});
            skLineSegment(sketch, "E115.0", {"start": v(-13.19, -31.9) * mm, "end": v(-13.19, -29.6) * mm});
            skLineSegment(sketch, "E116.0", {"start": v(-13.7, -31.9) * mm, "end": v(-13.7, -29.6) * mm});
            skLineSegment(sketch, "E117", {"start": v(-13.19, -33.61) * mm, "end": v(-13.19, -35.93) * mm});
            skLineSegment(sketch, "E118", {"start": v(-13.7, -33.61) * mm, "end": v(-13.7, -35.93) * mm});
            skArc(sketch, "E119.trimOffspring", {"start": v(-13.19, -33.61) * mm, "mid": v(-13.1, -33.58) * mm, "end": v(-13.02, -33.54) * mm});
            skArc(sketch, "E120.trimOffspring", {"start": v(-13.19, -35.93) * mm, "mid": v(-12.23, -35.7) * mm, "end": v(-11.38, -35.18) * mm});
            skLineSegment(sketch, "E121.0", {"start": v(-18.14, -33.01) * mm, "end": v(-18.14, -33.01) * mm});
            skLineSegment(sketch, "E122.0", {"start": v(-18.14, -32.5) * mm, "end": v(-18.14, -32.5) * mm});
            skLineSegment(sketch, "E123.trimOffspring", {"start": v(-16.61, -32.5) * mm, "end": v(-14.3, -32.5) * mm});
            skLineSegment(sketch, "E124.trimOffspring", {"start": v(-16.61, -33.01) * mm, "end": v(-14.3, -33.01) * mm});
            skLineSegment(sketch, "E125.trimOffspring", {"start": v(-8.75, -32.5) * mm, "end": v(-8.74, -32.5) * mm});
            skLineSegment(sketch, "E126.trimOffspring", {"start": v(-8.75, -33.01) * mm, "end": v(-8.74, -33.01) * mm});
            skLineSegment(sketch, "E127.trimOffspring", {"start": v(-12.59, -32.5) * mm, "end": v(-10.27, -32.5) * mm});
            skLineSegment(sketch, "E128.trimOffspring", {"start": v(-12.59, -33.01) * mm, "end": v(-10.27, -33.01) * mm});
            skArc(sketch, "E129.trimOffspring", {"start": v(-16.61, -33.01) * mm, "mid": v(-16.38, -33.98) * mm, "end": v(-15.86, -34.82) * mm});
            skArc(sketch, "E130.trimOffspring", {"start": v(-10.27, -32.5) * mm, "mid": v(-10.5, -31.54) * mm, "end": v(-11.02, -30.7) * mm});
            skArc(sketch, "E131.trimOffspring", {"start": v(-14.3, -33.01) * mm, "mid": v(-14.26, -33.1) * mm, "end": v(-14.22, -33.18) * mm});
            skLineSegment(sketch, "E132.0", {"start": v(-11.37, -30.33) * mm, "end": v(-13.02, -31.98) * mm});
            skLineSegment(sketch, "E133.0", {"start": v(-11.01, -30.7) * mm, "end": v(-12.66, -32.34) * mm});
            skLineSegment(sketch, "E134.trimOffspring", {"start": v(-14.22, -33.18) * mm, "end": v(-15.87, -34.83) * mm});
            skLineSegment(sketch, "E135.trimOffspring", {"start": v(-13.87, -33.54) * mm, "end": v(-15.51, -35.19) * mm});
            skArc(sketch, "E136.trimOffspring", {"start": v(-13.87, -33.54) * mm, "mid": v(-13.78, -33.58) * mm, "end": v(-13.7, -33.61) * mm});
            skArc(sketch, "E137.trimOffspring", {"start": v(-13.02, -31.98) * mm, "mid": v(-13.1, -31.94) * mm, "end": v(-13.19, -31.9) * mm});
            skArc(sketch, "E138.trimOffspring", {"start": v(-15.5, -35.18) * mm, "mid": v(-14.66, -35.7) * mm, "end": v(-13.7, -35.93) * mm});
            skArc(sketch, "E139.trimOffspring", {"start": v(-11.38, -30.34) * mm, "mid": v(-12.23, -29.82) * mm, "end": v(-13.19, -29.6) * mm});
            skArc(sketch, "E140.trimOffspring", {"start": v(-12.59, -32.5) * mm, "mid": v(-12.62, -32.42) * mm, "end": v(-12.66, -32.34) * mm});
            skLineSegment(sketch, "E141.0", {"start": v(-15.87, -30.7) * mm, "end": v(-14.22, -32.34) * mm});
            skLineSegment(sketch, "E142.0", {"start": v(-15.51, -30.33) * mm, "end": v(-13.87, -31.98) * mm});
            skArc(sketch, "E143.trimOffspring", {"start": v(-14.22, -32.34) * mm, "mid": v(-14.26, -32.42) * mm, "end": v(-14.3, -32.5) * mm});
            skLineSegment(sketch, "E144.trimOffspring", {"start": v(-13.02, -33.54) * mm, "end": v(-11.37, -35.19) * mm});
            skLineSegment(sketch, "E145.trimOffspring", {"start": v(-12.66, -33.18) * mm, "end": v(-11.01, -34.83) * mm});
            skArc(sketch, "E146.trimOffspring", {"start": v(-12.66, -33.18) * mm, "mid": v(-12.62, -33.1) * mm, "end": v(-12.59, -33.01) * mm});
            skArc(sketch, "E147.trimOffspring", {"start": v(-15.86, -30.7) * mm, "mid": v(-16.38, -31.54) * mm, "end": v(-16.61, -32.5) * mm});
            skArc(sketch, "E148.trimOffspring", {"start": v(-11.02, -34.82) * mm, "mid": v(-10.5, -33.98) * mm, "end": v(-10.27, -33.01) * mm});
            skCircle(sketch, "E149", {"center": v(-13.44, -32.76) * mm, "radius": 0.64 * mm});
            skSolve(sketch);
        }
        {
            var Q0;
            Q0 = qSketchRegion(id + "F42", true);
            extrude(context, id + "F43", {"entities" : qUnion([Q0]), "depth" : 1.27 * mm, "offsetDistance" : 25.4 * mm});
        }
        {
            var Q0;
            Q0=makeQuery(id+"F39.opExtrude","CAP_FACE",FACE,{"disambiguationData":[OSD([sQuery(id+"F38.wireOp",EDGE,"E110")])],"isStart":false});
            var sketch = newSketch(context, id + "F44", { "sketchPlane" : qUnion([Q0])});
            skCircle(sketch, "E150", {"center": v(13.44, -32.76) * mm, "radius": 4.7 * mm});
            skArc(sketch, "E151.0", {"start": v(13.19, -29.6) * mm, "mid": v(12.23, -29.82) * mm, "end": v(11.38, -30.34) * mm});
            skArc(sketch, "E152", {"start": v(13.19, -31.9) * mm, "mid": v(13.1, -31.94) * mm, "end": v(13.02, -31.98) * mm});
            skLineSegment(sketch, "E153.0", {"start": v(13.7, -31.9) * mm, "end": v(13.7, -29.6) * mm});
            skLineSegment(sketch, "E154.0", {"start": v(13.19, -31.9) * mm, "end": v(13.19, -29.6) * mm});
            skLineSegment(sketch, "E155", {"start": v(13.7, -33.61) * mm, "end": v(13.7, -35.93) * mm});
            skLineSegment(sketch, "E156", {"start": v(13.19, -33.61) * mm, "end": v(13.19, -35.93) * mm});
            skArc(sketch, "E157.trimOffspring", {"start": v(13.7, -33.61) * mm, "mid": v(13.78, -33.58) * mm, "end": v(13.87, -33.54) * mm});
            skArc(sketch, "E158.trimOffspring", {"start": v(13.7, -35.93) * mm, "mid": v(14.66, -35.7) * mm, "end": v(15.5, -35.18) * mm});
            skLineSegment(sketch, "E159.0", {"start": v(8.74, -33.01) * mm, "end": v(8.75, -33.01) * mm});
            skLineSegment(sketch, "E160.0", {"start": v(8.74, -32.5) * mm, "end": v(8.75, -32.5) * mm});
            skLineSegment(sketch, "E161.trimOffspring", {"start": v(10.27, -32.5) * mm, "end": v(12.59, -32.5) * mm});
            skLineSegment(sketch, "E162.trimOffspring", {"start": v(10.27, -33.01) * mm, "end": v(12.59, -33.01) * mm});
            skLineSegment(sketch, "E163.trimOffspring", {"start": v(18.14, -32.5) * mm, "end": v(18.14, -32.5) * mm});
            skLineSegment(sketch, "E164.trimOffspring", {"start": v(18.14, -33.01) * mm, "end": v(18.14, -33.01) * mm});
            skLineSegment(sketch, "E165.trimOffspring", {"start": v(14.3, -32.5) * mm, "end": v(16.61, -32.5) * mm});
            skLineSegment(sketch, "E166.trimOffspring", {"start": v(14.3, -33.01) * mm, "end": v(16.61, -33.01) * mm});
            skArc(sketch, "E167.trimOffspring", {"start": v(10.27, -33.01) * mm, "mid": v(10.5, -33.98) * mm, "end": v(11.02, -34.82) * mm});
            skArc(sketch, "E168.trimOffspring", {"start": v(16.61, -32.5) * mm, "mid": v(16.38, -31.54) * mm, "end": v(15.86, -30.7) * mm});
            skArc(sketch, "E169.trimOffspring", {"start": v(12.59, -33.01) * mm, "mid": v(12.62, -33.1) * mm, "end": v(12.66, -33.18) * mm});
            skLineSegment(sketch, "E170.0", {"start": v(15.51, -30.33) * mm, "end": v(13.87, -31.98) * mm});
            skLineSegment(sketch, "E171.0", {"start": v(15.87, -30.7) * mm, "end": v(14.22, -32.34) * mm});
            skLineSegment(sketch, "E172.trimOffspring", {"start": v(12.66, -33.18) * mm, "end": v(11.01, -34.83) * mm});
            skLineSegment(sketch, "E173.trimOffspring", {"start": v(13.02, -33.54) * mm, "end": v(11.37, -35.19) * mm});
            skArc(sketch, "E174.trimOffspring", {"start": v(13.02, -33.54) * mm, "mid": v(13.1, -33.58) * mm, "end": v(13.19, -33.61) * mm});
            skArc(sketch, "E175.trimOffspring", {"start": v(13.87, -31.98) * mm, "mid": v(13.78, -31.94) * mm, "end": v(13.7, -31.9) * mm});
            skArc(sketch, "E176.trimOffspring", {"start": v(11.38, -35.18) * mm, "mid": v(12.23, -35.7) * mm, "end": v(13.19, -35.93) * mm});
            skArc(sketch, "E177.trimOffspring", {"start": v(15.5, -30.34) * mm, "mid": v(14.66, -29.82) * mm, "end": v(13.7, -29.6) * mm});
            skArc(sketch, "E178.trimOffspring", {"start": v(14.3, -32.5) * mm, "mid": v(14.26, -32.42) * mm, "end": v(14.22, -32.34) * mm});
            skLineSegment(sketch, "E179.0", {"start": v(11.01, -30.7) * mm, "end": v(12.66, -32.34) * mm});
            skLineSegment(sketch, "E180.0", {"start": v(11.37, -30.33) * mm, "end": v(13.02, -31.98) * mm});
            skArc(sketch, "E181.trimOffspring", {"start": v(12.66, -32.34) * mm, "mid": v(12.62, -32.42) * mm, "end": v(12.59, -32.5) * mm});
            skLineSegment(sketch, "E182.trimOffspring", {"start": v(13.87, -33.54) * mm, "end": v(15.51, -35.19) * mm});
            skLineSegment(sketch, "E183.trimOffspring", {"start": v(14.22, -33.18) * mm, "end": v(15.87, -34.83) * mm});
            skArc(sketch, "E184.trimOffspring", {"start": v(14.22, -33.18) * mm, "mid": v(14.26, -33.1) * mm, "end": v(14.3, -33.01) * mm});
            skArc(sketch, "E185.trimOffspring", {"start": v(11.02, -30.7) * mm, "mid": v(10.5, -31.54) * mm, "end": v(10.27, -32.5) * mm});
            skArc(sketch, "E186.trimOffspring", {"start": v(15.86, -34.82) * mm, "mid": v(16.38, -33.98) * mm, "end": v(16.61, -33.01) * mm});
            skCircle(sketch, "E187", {"center": v(13.44, -32.76) * mm, "radius": 0.64 * mm});
            skSolve(sketch);
        }
        {
            var Q0;
            Q0=makeQuery(id+"F41.opExtrude","CAP_FACE",FACE,{"disambiguationData":[OSD([sQuery(id+"F40.wireOp",EDGE,"E111")])],"isStart":false});
            var sketch = newSketch(context, id + "F45", { "sketchPlane" : qUnion([Q0])});
            skCircle(sketch, "E188", {"center": v(-13.44, -32.76) * mm, "radius": 4.7 * mm});
            skArc(sketch, "E189.0", {"start": v(-13.7, -29.6) * mm, "mid": v(-14.66, -29.82) * mm, "end": v(-15.5, -30.34) * mm});
            skArc(sketch, "E190", {"start": v(-13.7, -31.9) * mm, "mid": v(-13.78, -31.94) * mm, "end": v(-13.87, -31.98) * mm});
            skLineSegment(sketch, "E191.0", {"start": v(-13.19, -31.9) * mm, "end": v(-13.19, -29.6) * mm});
            skLineSegment(sketch, "E192.0", {"start": v(-13.7, -31.9) * mm, "end": v(-13.7, -29.6) * mm});
            skLineSegment(sketch, "E193", {"start": v(-13.19, -33.61) * mm, "end": v(-13.19, -35.93) * mm});
            skLineSegment(sketch, "E194", {"start": v(-13.7, -33.61) * mm, "end": v(-13.7, -35.93) * mm});
            skArc(sketch, "E195.trimOffspring", {"start": v(-13.19, -33.61) * mm, "mid": v(-13.1, -33.58) * mm, "end": v(-13.02, -33.54) * mm});
            skArc(sketch, "E196.trimOffspring", {"start": v(-13.19, -35.93) * mm, "mid": v(-12.23, -35.7) * mm, "end": v(-11.38, -35.18) * mm});
            skLineSegment(sketch, "E197.0", {"start": v(-18.14, -33.01) * mm, "end": v(-18.14, -33.01) * mm});
            skLineSegment(sketch, "E198.0", {"start": v(-18.14, -32.5) * mm, "end": v(-18.14, -32.5) * mm});
            skLineSegment(sketch, "E199.trimOffspring", {"start": v(-16.61, -32.5) * mm, "end": v(-14.3, -32.5) * mm});
            skLineSegment(sketch, "E200.trimOffspring", {"start": v(-16.61, -33.01) * mm, "end": v(-14.3, -33.01) * mm});
            skLineSegment(sketch, "E201.trimOffspring", {"start": v(-8.75, -32.5) * mm, "end": v(-8.74, -32.5) * mm});
            skLineSegment(sketch, "E202.trimOffspring", {"start": v(-8.75, -33.01) * mm, "end": v(-8.74, -33.01) * mm});
            skLineSegment(sketch, "E203.trimOffspring", {"start": v(-12.59, -32.5) * mm, "end": v(-10.27, -32.5) * mm});
            skLineSegment(sketch, "E204.trimOffspring", {"start": v(-12.59, -33.01) * mm, "end": v(-10.27, -33.01) * mm});
            skArc(sketch, "E205.trimOffspring", {"start": v(-16.61, -33.01) * mm, "mid": v(-16.38, -33.98) * mm, "end": v(-15.86, -34.82) * mm});
            skArc(sketch, "E206.trimOffspring", {"start": v(-10.27, -32.5) * mm, "mid": v(-10.5, -31.54) * mm, "end": v(-11.02, -30.7) * mm});
            skArc(sketch, "E207.trimOffspring", {"start": v(-14.3, -33.01) * mm, "mid": v(-14.26, -33.1) * mm, "end": v(-14.22, -33.18) * mm});
            skLineSegment(sketch, "E208.0", {"start": v(-11.37, -30.33) * mm, "end": v(-13.02, -31.98) * mm});
            skLineSegment(sketch, "E209.0", {"start": v(-11.01, -30.7) * mm, "end": v(-12.66, -32.34) * mm});
            skLineSegment(sketch, "E210.trimOffspring", {"start": v(-14.22, -33.18) * mm, "end": v(-15.87, -34.83) * mm});
            skLineSegment(sketch, "E211.trimOffspring", {"start": v(-13.87, -33.54) * mm, "end": v(-15.51, -35.19) * mm});
            skArc(sketch, "E212.trimOffspring", {"start": v(-13.87, -33.54) * mm, "mid": v(-13.78, -33.58) * mm, "end": v(-13.7, -33.61) * mm});
            skArc(sketch, "E213.trimOffspring", {"start": v(-13.02, -31.98) * mm, "mid": v(-13.1, -31.94) * mm, "end": v(-13.19, -31.9) * mm});
            skArc(sketch, "E214.trimOffspring", {"start": v(-15.5, -35.18) * mm, "mid": v(-14.66, -35.7) * mm, "end": v(-13.7, -35.93) * mm});
            skArc(sketch, "E215.trimOffspring", {"start": v(-11.38, -30.34) * mm, "mid": v(-12.23, -29.82) * mm, "end": v(-13.19, -29.6) * mm});
            skArc(sketch, "E216.trimOffspring", {"start": v(-12.59, -32.5) * mm, "mid": v(-12.62, -32.42) * mm, "end": v(-12.66, -32.34) * mm});
            skLineSegment(sketch, "E217.0", {"start": v(-15.87, -30.7) * mm, "end": v(-14.22, -32.34) * mm});
            skLineSegment(sketch, "E218.0", {"start": v(-15.51, -30.33) * mm, "end": v(-13.87, -31.98) * mm});
            skArc(sketch, "E219.trimOffspring", {"start": v(-14.22, -32.34) * mm, "mid": v(-14.26, -32.42) * mm, "end": v(-14.3, -32.5) * mm});
            skLineSegment(sketch, "E220.trimOffspring", {"start": v(-13.02, -33.54) * mm, "end": v(-11.37, -35.19) * mm});
            skLineSegment(sketch, "E221.trimOffspring", {"start": v(-12.66, -33.18) * mm, "end": v(-11.01, -34.83) * mm});
            skArc(sketch, "E222.trimOffspring", {"start": v(-12.66, -33.18) * mm, "mid": v(-12.62, -33.1) * mm, "end": v(-12.59, -33.01) * mm});
            skArc(sketch, "E223.trimOffspring", {"start": v(-15.86, -30.7) * mm, "mid": v(-16.38, -31.54) * mm, "end": v(-16.61, -32.5) * mm});
            skArc(sketch, "E224.trimOffspring", {"start": v(-11.02, -34.82) * mm, "mid": v(-10.5, -33.98) * mm, "end": v(-10.27, -33.01) * mm});
            skCircle(sketch, "E225", {"center": v(-13.44, -32.76) * mm, "radius": 0.64 * mm});
            skSolve(sketch);
        }
        {
            var Q0;
            Q0 = qSketchRegion(id + "F45", true);
            extrude(context, id + "F46", {"entities" : qUnion([Q0]), "depth" : 1.27 * mm, "offsetDistance" : 25.4 * mm});
        }
        {
            var Q0;
            Q0 = qSketchRegion(id + "F44", true);
            extrude(context, id + "F47", {"entities" : qUnion([Q0]), "depth" : 1.27 * mm, "offsetDistance" : 25.4 * mm});
        }
        {
            var Q0;
            Q0=makeQuery(id+"F33.opExtrude","CAP_EDGE",EDGE,{"disambiguationData":[OSD([sQuery(id+"F32.wireOp",EDGE,"E104")])],"isStart":false});
            chamfer(context, id + "F48", {"entities" : qUnion([Q0]), "width" : 15.24 * mm, "tangentPropagation" : true});
        }
        {
            var Q0;
            Q0=qCreatedBy(makeId("Right.planeOp"),FACE);
            cPlane(context, id + "F49", {"entities" : qUnion([Q0]), "cplaneType" : CPlaneType.OFFSET, "offset" : 30.73 * mm, "width" : 152.4 * mm, "height" : 152.4 * mm});
        }
        {
            var Q0;
            Q0=qCreatedBy(id+"F49.planeOp",FACE);
            var sketch = newSketch(context, id + "F50", { "sketchPlane" : qUnion([Q0])});
            skLineSegment(sketch, "E226.bottom", {"start": v(23.48, -15.37) * mm, "end": v(-13.92, -15.37) * mm});
            skLineSegment(sketch, "E226.top", {"start": v(23.48, -17.05) * mm, "end": v(-13.92, -17.05) * mm});
            skLineSegment(sketch, "E226.left", {"start": v(23.48, -15.37) * mm, "end": v(23.48, -17.05) * mm});
            skPoint(sketch, "E226.middle", {"position": v(0.02, -16.21) * mm});
            skLineSegment(sketch, "E227", {"start": v(-13.92, -15.37) * mm, "end": v(-13.92, -17.05) * mm});
            skSolve(sketch);
        }
        {
            var Q0;
            Q0=makeQuery(id+"F50.imprint","IMPRINT",FACE,{"disambiguationData":[TD([[makeQuery(id+"F50.imprint","IMPRINT",EDGE,{"derivedFrom":sQuery(id+"F50.wireOp",EDGE,"E226.bottom")}),1.0]])]});
            extrude(context, id + "F51", {"entities" : qUnion([Q0]), "operationType" : NewBodyOperationType.ADD, "depth" : 12.7 * mm, "offsetDistance" : 25.4 * mm});
        }
        {
            var Q0;
            {var subQ0=sQuery(id+"F50.wireOp",EDGE,"E226.top");var subQ1=sQuery(id+"F50.wireOp",EDGE,"E226.bottom");var subQ2=sQuery(id+"F50.wireOp",EDGE,"E227");Q0=makeQuery(id+"F51.boolean.opBoolean","SPLIT",FACE,{"disambiguationData":[TD([makeQuery(id+"F51.opExtrude","SWEPT_FACE",FACE,{"disambiguationData":[OSD([subQ2])]})])],"derivedFrom":makeQuery(id+"F51.opExtrude","CAP_FACE",FACE,{"disambiguationData":[OSD([subQ1,subQ0,sQuery(id+"F50.wireOp",EDGE,"E226.left"),subQ2])],"isStart":true})});}
            var sketch = newSketch(context, id + "F52", { "sketchPlane" : qUnion([Q0])});
            skLineSegment(sketch, "E228", {"start": v(13.92, -15.37) * mm, "end": v(13.92, -17.05) * mm});
            skLineSegment(sketch, "E229", {"start": v(13.92, -17.05) * mm, "end": v(6, -17.05) * mm});
            skLineSegment(sketch, "E230", {"start": v(6, -17.05) * mm, "end": v(8.48, -15.37) * mm});
            skLineSegment(sketch, "E231", {"start": v(8.48, -15.37) * mm, "end": v(13.92, -15.37) * mm});
            skSolve(sketch);
        }
        {
            var Q0;
            Q0 = qSketchRegion(id + "F52", true);
            extrude(context, id + "F53", {"entities" : qUnion([Q0]), "operationType" : NewBodyOperationType.ADD, "depth" : 3.48 * mm, "offsetDistance" : 25.4 * mm});
        }
        {
            var Q0;
            Q0=makeQuery(id+"F51.opExtrude","CAP_EDGE",EDGE,{"disambiguationData":[OSD([sQuery(id+"F50.wireOp",EDGE,"E227")])],"isStart":false});
            chamfer(context, id + "F54", {"entities" : qUnion([Q0]), "width" : 15.24 * mm, "tangentPropagation" : true});
        }
        {
            var Q0;
            Q0=qCreatedBy(makeId("Front.planeOp"),FACE);
            cPlane(context, id + "F55", {"entities" : qUnion([Q0]), "cplaneType" : CPlaneType.OFFSET, "offset" : 29.2 * mm, "oppositeDirection" : true, "width" : 152.4 * mm, "height" : 152.4 * mm});
        }
        {
            var Q0;
            Q0=qCreatedBy(id+"F55.planeOp",FACE);
            var sketch = newSketch(context, id + "F56", { "sketchPlane" : qUnion([Q0])});
            skLineSegment(sketch, "E232", {"start": v(11.29, 12.84) * mm, "end": v(-10.3, 12.84) * mm});
            skArc(sketch, "E233", {"start": v(11.29, 12.84) * mm, "mid": v(0.5, 22.2) * mm, "end": v(-10.3, 12.84) * mm});
            skSolve(sketch);
        }
        {
            var Q0;
            Q0 = qSketchRegion(id + "F56", true);
            extrude(context, id + "F57", {"entities" : qUnion([Q0]), "operationType" : NewBodyOperationType.REMOVE, "endBound" : BoundingType.SYMMETRIC, "oppositeDirection" : true, "depth" : 25.4 * mm, "offsetDistance" : 25.4 * mm});
        }
        {
            var Q0;
            Q0=qCreatedBy(makeId("Top.planeOp"),FACE);
            cPlane(context, id + "F58", {"entities" : qUnion([Q0]), "cplaneType" : CPlaneType.OFFSET, "offset" : 4.57 * mm, "oppositeDirection" : true, "width" : 152.4 * mm, "height" : 152.4 * mm});
        }
        {
            var Q0;
            Q0=qCreatedBy(id+"F58.planeOp",FACE);
            var sketch = newSketch(context, id + "F59", { "sketchPlane" : qUnion([Q0])});
            skCircle(sketch, "E234", {"center": v(0, 0) * mm, "radius": 34.38 * mm});
            skSolve(sketch);
        }
        {
            var Q0;
            Q0 = qSketchRegion(id + "F59", true);
            extrude(context, id + "F60", {"entities" : qUnion([Q0]), "operationType" : NewBodyOperationType.ADD, "endBound" : BoundingType.SYMMETRIC, "depth" : 2.54 * mm, "offsetDistance" : 25.4 * mm});
        }
    });
